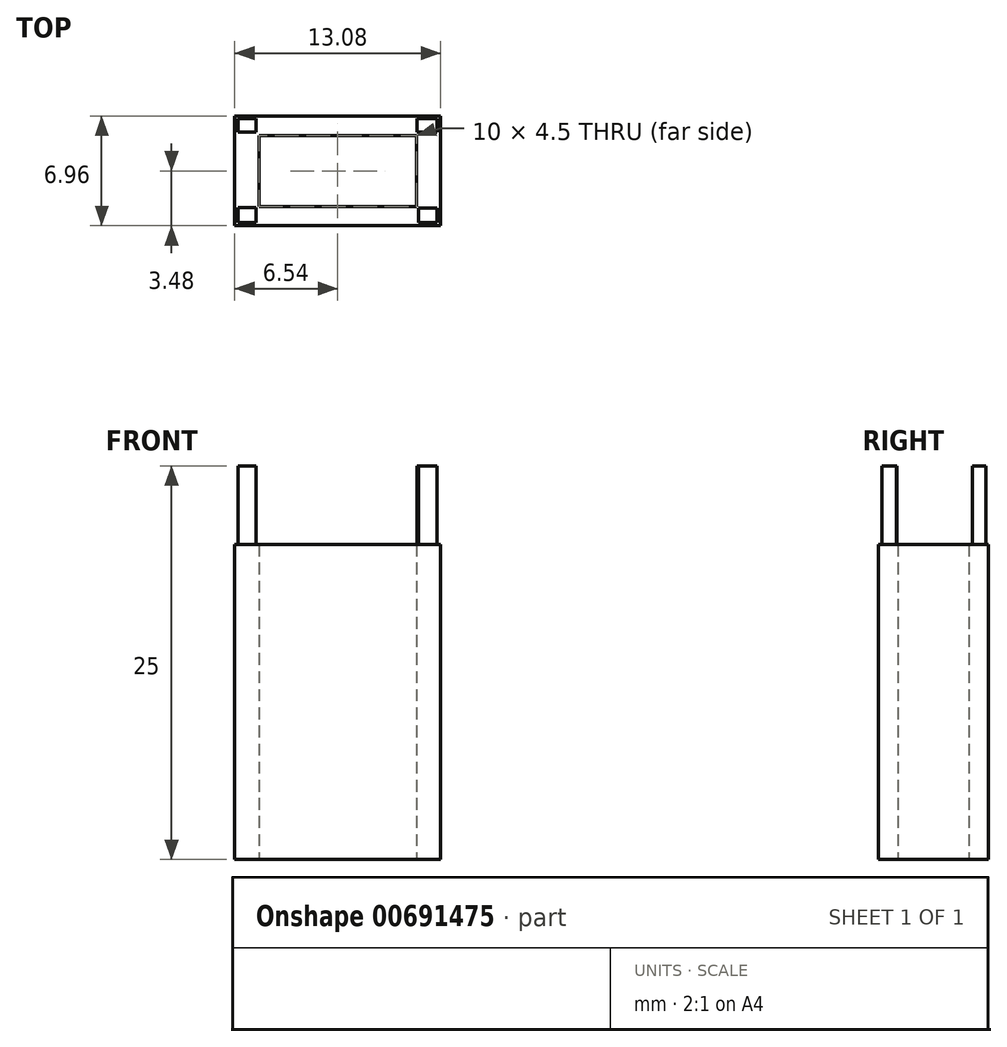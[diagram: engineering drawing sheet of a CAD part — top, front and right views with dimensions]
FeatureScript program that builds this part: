
annotation { "Feature Type Name" : "Feature", "Feature Type Description" : "" }
export const myFeature = defineFeature(function(context is Context, id is Id, definition is map)
    precondition{}
    {
        {
            var Q0;
            Q0=qCreatedBy(makeId("Top.planeOp"),FACE);
            var sketch = newSketch(context, id + "F0", { "sketchPlane" : qUnion([Q0])});
            skLineSegment(sketch, "E0.bottom", {"start": v(5, 2.25) * mm, "end": v(-5, 2.25) * mm});
            skLineSegment(sketch, "E0.top", {"start": v(5, -2.25) * mm, "end": v(-5, -2.25) * mm});
            skLineSegment(sketch, "E0.left", {"start": v(5, 2.25) * mm, "end": v(5, -2.25) * mm});
            skLineSegment(sketch, "E0.right", {"start": v(-5, 2.25) * mm, "end": v(-5, -2.25) * mm});
            skPoint(sketch, "E0.middle", {"position": v(0, 0) * mm});
            skLineSegment(sketch, "E1.bottom", {"start": v(6.54, 3.48) * mm, "end": v(-6.54, 3.48) * mm});
            skLineSegment(sketch, "E1.top", {"start": v(6.54, -3.48) * mm, "end": v(-6.54, -3.48) * mm});
            skLineSegment(sketch, "E1.left", {"start": v(6.54, 3.48) * mm, "end": v(6.54, -3.48) * mm});
            skLineSegment(sketch, "E1.right", {"start": v(-6.54, 3.48) * mm, "end": v(-6.54, -3.48) * mm});
            skSolve(sketch);
        }
        {
            var Q0;
            Q0=makeQuery(id+"F0.imprint","IMPRINT",FACE,{"disambiguationData":[TD([[makeQuery(id+"F0.imprint","IMPRINT",EDGE,{"derivedFrom":sQuery(id+"F0.wireOp",EDGE,"E0.bottom")}),-1.0]])]});
            extrude(context, id + "F1", {"entities" : qUnion([Q0]), "depth" : 20 * mm, "offsetDistance" : 25.4 * mm});
        }
        {
            var Q0;
            Q0=qCreatedBy(makeId("Top.planeOp"),FACE);
            var sketch = newSketch(context, id + "F2", { "sketchPlane" : qUnion([Q0])});
            skLineSegment(sketch, "E2.bottom", {"start": v(-5.17, 2.47) * mm, "end": v(-6.33, 2.47) * mm});
            skLineSegment(sketch, "E2.top", {"start": v(-5.17, 3.33) * mm, "end": v(-6.33, 3.33) * mm});
            skLineSegment(sketch, "E2.left", {"start": v(-5.17, 2.47) * mm, "end": v(-5.17, 3.33) * mm});
            skLineSegment(sketch, "E2.right", {"start": v(-6.33, 2.47) * mm, "end": v(-6.33, 3.33) * mm});
            skPoint(sketch, "E3.oppositeSnap0", {"position": v(-6.33, 2.9) * mm});
            skLineSegment(sketch, "E3.bottom", {"start": v(-5.17, -2.32) * mm, "end": v(-6.33, -2.32) * mm});
            skLineSegment(sketch, "E3.top", {"start": v(-5.17, -3.27) * mm, "end": v(-6.33, -3.27) * mm});
            skLineSegment(sketch, "E3.left", {"start": v(-5.17, -2.32) * mm, "end": v(-5.17, -3.27) * mm});
            skLineSegment(sketch, "E3.right", {"start": v(-6.33, -2.32) * mm, "end": v(-6.33, -3.27) * mm});
            skPoint(sketch, "E4.oppositeSnap0", {"position": v(-5.75, -3.27) * mm});
            skLineSegment(sketch, "E4.bottom", {"start": v(5.15, -2.35) * mm, "end": v(6.3, -2.35) * mm});
            skLineSegment(sketch, "E4.top", {"start": v(5.15, -3.27) * mm, "end": v(6.3, -3.27) * mm});
            skLineSegment(sketch, "E4.left", {"start": v(5.15, -2.35) * mm, "end": v(5.15, -3.27) * mm});
            skLineSegment(sketch, "E4.right", {"start": v(6.3, -2.35) * mm, "end": v(6.3, -3.27) * mm});
            skLineSegment(sketch, "E5.bottom", {"start": v(5.06, 3.33) * mm, "end": v(6.3, 3.33) * mm});
            skLineSegment(sketch, "E5.top", {"start": v(5.06, 2.47) * mm, "end": v(6.3, 2.47) * mm});
            skLineSegment(sketch, "E5.left", {"start": v(5.06, 3.33) * mm, "end": v(5.06, 2.47) * mm});
            skLineSegment(sketch, "E5.right", {"start": v(6.3, 3.33) * mm, "end": v(6.3, 2.47) * mm});
            skSolve(sketch);
        }
        {
            var Q0;
            Q0 = qSketchRegion(id + "F2", true);
            extrude(context, id + "F3", {"entities" : qUnion([Q0]), "operationType" : NewBodyOperationType.ADD, "depth" : 25 * mm, "offsetDistance" : 25.4 * mm});
        }
    });
